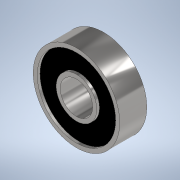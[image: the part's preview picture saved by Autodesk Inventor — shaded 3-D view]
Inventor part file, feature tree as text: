
AUTODESK INVENTOR PART (.ipt)
format: ipt  version: 2022 (Build 260153000, 153)  size: 147,968 bytes
history: native  units: mm
features: extrude x2, sketch x2, plane x1, mirror x1, projected_geometry x1
ambient origin geometry x8: Origin, YZ Plane, XZ Plane, XY Plane, X Axis, Y Axis, Z Axis, Center Point
bodies: Solid1 (feature_tree)
feature tree (7):
  extrude  "Extrusion1"  Depth=32.0mm
  extrude  "Extrusion2"  Depth=1.0mm
  plane  "Work Plane1"
  mirror  "Mirror1"
  sketch  "Sketch1"  dims[d0=12.0mm d1=32.0mm]
  sketch  "Sketch2"  dims[d2=10.0mm d3=0.0mm d4=1.5mm d5=1.5mm d6=1.0mm d7=0.0mm]
  projected_geometry  "Projected Loop1"
